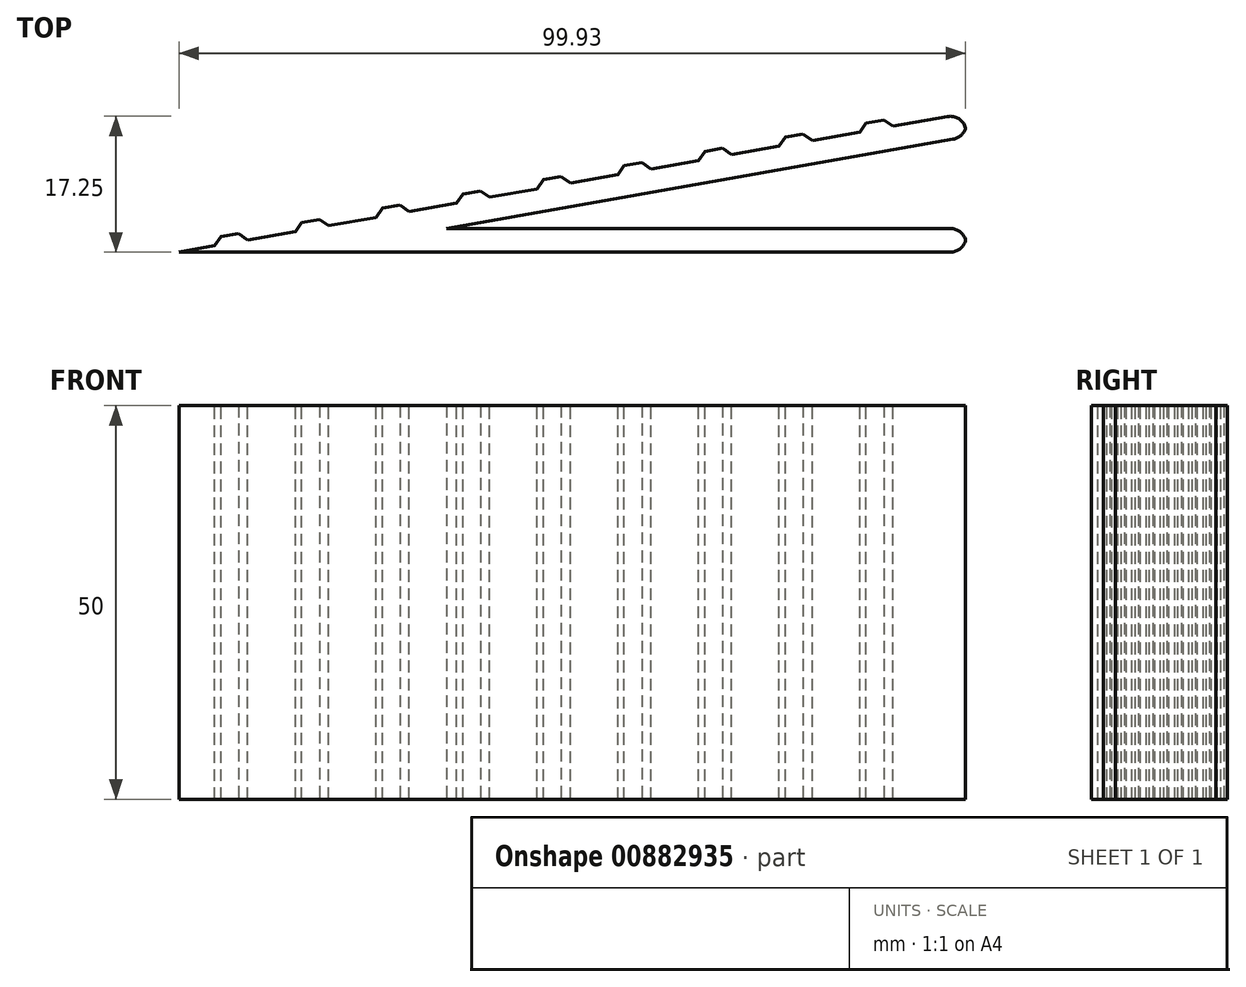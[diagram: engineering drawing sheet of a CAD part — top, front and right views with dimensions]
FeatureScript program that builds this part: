
annotation { "Feature Type Name" : "Feature", "Feature Type Description" : "" }
export const myFeature = defineFeature(function(context is Context, id is Id, definition is map)
    precondition{}
    {
        {
            var Q0;
            Q0=qCreatedBy(makeId("Top.planeOp"),FACE);
            var sketch = newSketch(context, id + "F0", { "sketchPlane" : qUnion([Q0])});
            skLineSegment(sketch, "E0", {"start": v(46.9, 0) * mm, "end": v(-53.1, 0) * mm});
            skLineSegment(sketch, "E1", {"start": v(-53.1, 0) * mm, "end": v(46.9, 17.63) * mm});
            skLineSegment(sketch, "E2", {"start": v(46.9, 3) * mm, "end": v(-19.07, 3) * mm});
            skLineSegment(sketch, "E3", {"start": v(-19.07, 3) * mm, "end": v(46.9, 14.63) * mm});
            skLineSegment(sketch, "E4", {"start": v(46.9, 14.63) * mm, "end": v(46.9, 17.63) * mm});
            skLineSegment(sketch, "E5", {"start": v(46.9, 3) * mm, "end": v(46.9, 0) * mm});
            skSolve(sketch);
        }
        {
            var Q0;
            Q0=makeQuery(id+"F0.imprint","IMPRINT",FACE,{"disambiguationData":[TD([[makeQuery(id+"F0.imprint","IMPRINT",EDGE,{"derivedFrom":sQuery(id+"F0.wireOp",EDGE,"E0")}),-1.0]])]});
            extrude(context, id + "F1", {"entities" : qUnion([Q0]), "depth" : 50 * mm, "offsetDistance" : 25 * mm});
        }
        {
            var Q0;
            Q0=makeQuery(id+"F1.opExtrude","SWEPT_EDGE",EDGE,{"disambiguationData":[OSD([sQuery(id+"F0.wireOp",EDGE,"E1"),sQuery(id+"F0.wireOp",EDGE,"E4")])]});
            var Q1;
            Q1=makeQuery(id+"F1.opExtrude","SWEPT_EDGE",EDGE,{"disambiguationData":[OSD([sQuery(id+"F0.wireOp",EDGE,"E3"),sQuery(id+"F0.wireOp",EDGE,"E4")])]});
            var Q2;
            Q2=makeQuery(id+"F1.opExtrude","SWEPT_EDGE",EDGE,{"disambiguationData":[OSD([sQuery(id+"F0.wireOp",EDGE,"E2"),sQuery(id+"F0.wireOp",EDGE,"E5")])]});
            var Q3;
            Q3=makeQuery(id+"F1.opExtrude","SWEPT_EDGE",EDGE,{"disambiguationData":[OSD([sQuery(id+"F0.wireOp",EDGE,"E0"),sQuery(id+"F0.wireOp",EDGE,"E5")])]});
            fillet(context, id + "F2", {"entities" : qUnion([Q0, Q1, Q2, Q3]), "radius" : 2 * mm, "tangentPropagation" : true, "allowEdgeOverflow" : false});
        }
        {
            var Q0;
            Q0=makeQuery(id+"F1.opExtrude","SWEPT_FACE",FACE,{"disambiguationData":[OSD([sQuery(id+"F0.wireOp",EDGE,"E1")])]});
            var sketch = newSketch(context, id + "F3", { "sketchPlane" : qUnion([Q0])});
            skLineSegment(sketch, "E6.bottom", {"start": v(47.67, 0) * mm, "end": v(43.4, 0) * mm});
            skLineSegment(sketch, "E6.top", {"start": v(47.67, 50) * mm, "end": v(43.4, 50) * mm});
            skLineSegment(sketch, "E6.left", {"start": v(47.67, 0) * mm, "end": v(47.67, 50) * mm});
            skLineSegment(sketch, "E6.right", {"start": v(43.4, 0) * mm, "end": v(43.4, 50) * mm});
            skLineSegment(sketch, "E7.1.0.0", {"start": v(33, 0) * mm, "end": v(33, 50) * mm});
            skLineSegment(sketch, "E7.1.0.1", {"start": v(37.27, 0) * mm, "end": v(37.27, 50) * mm});
            skLineSegment(sketch, "E7.1.0.2", {"start": v(37.27, 0) * mm, "end": v(33, 0) * mm});
            skLineSegment(sketch, "E7.1.0.3", {"start": v(37.27, 50) * mm, "end": v(33, 50) * mm});
            skLineSegment(sketch, "E7.2.0.0", {"start": v(22.6, 0) * mm, "end": v(22.6, 50) * mm});
            skLineSegment(sketch, "E7.2.0.1", {"start": v(26.87, 0) * mm, "end": v(26.87, 50) * mm});
            skLineSegment(sketch, "E7.2.0.2", {"start": v(26.87, 0) * mm, "end": v(22.6, 0) * mm});
            skLineSegment(sketch, "E7.2.0.3", {"start": v(26.87, 50) * mm, "end": v(22.6, 50) * mm});
            skLineSegment(sketch, "E7.3.0.0", {"start": v(12.2, 0) * mm, "end": v(12.2, 50) * mm});
            skLineSegment(sketch, "E7.3.0.1", {"start": v(16.47, 0) * mm, "end": v(16.47, 50) * mm});
            skLineSegment(sketch, "E7.3.0.2", {"start": v(16.47, 0) * mm, "end": v(12.2, 0) * mm});
            skLineSegment(sketch, "E7.3.0.3", {"start": v(16.47, 50) * mm, "end": v(12.2, 50) * mm});
            skLineSegment(sketch, "E7.4.0.0", {"start": v(1.8, 0) * mm, "end": v(1.8, 50) * mm});
            skLineSegment(sketch, "E7.4.0.1", {"start": v(6.07, 0) * mm, "end": v(6.07, 50) * mm});
            skLineSegment(sketch, "E7.4.0.2", {"start": v(6.07, 0) * mm, "end": v(1.8, 0) * mm});
            skLineSegment(sketch, "E7.4.0.3", {"start": v(6.07, 50) * mm, "end": v(1.8, 50) * mm});
            skLineSegment(sketch, "E7.5.0.0", {"start": v(-8.6, 0) * mm, "end": v(-8.6, 50) * mm});
            skLineSegment(sketch, "E7.5.0.1", {"start": v(-4.33, 0) * mm, "end": v(-4.33, 50) * mm});
            skLineSegment(sketch, "E7.5.0.2", {"start": v(-4.33, 0) * mm, "end": v(-8.6, 0) * mm});
            skLineSegment(sketch, "E7.5.0.3", {"start": v(-4.33, 50) * mm, "end": v(-8.6, 50) * mm});
            skLineSegment(sketch, "E7.6.0.0", {"start": v(-19, 0) * mm, "end": v(-19, 50) * mm});
            skLineSegment(sketch, "E7.6.0.1", {"start": v(-14.73, 0) * mm, "end": v(-14.73, 50) * mm});
            skLineSegment(sketch, "E7.6.0.2", {"start": v(-14.73, 0) * mm, "end": v(-19, 0) * mm});
            skLineSegment(sketch, "E7.6.0.3", {"start": v(-14.73, 50) * mm, "end": v(-19, 50) * mm});
            skLineSegment(sketch, "E7.7.0.0", {"start": v(-29.4, 0) * mm, "end": v(-29.4, 50) * mm});
            skLineSegment(sketch, "E7.7.0.1", {"start": v(-25.13, 0) * mm, "end": v(-25.13, 50) * mm});
            skLineSegment(sketch, "E7.7.0.2", {"start": v(-25.13, 0) * mm, "end": v(-29.4, 0) * mm});
            skLineSegment(sketch, "E7.7.0.3", {"start": v(-25.13, 50) * mm, "end": v(-29.4, 50) * mm});
            skLineSegment(sketch, "E7.8.0.0", {"start": v(-39.8, 0) * mm, "end": v(-39.8, 50) * mm});
            skLineSegment(sketch, "E7.8.0.1", {"start": v(-35.53, 0) * mm, "end": v(-35.53, 50) * mm});
            skLineSegment(sketch, "E7.8.0.2", {"start": v(-35.53, 0) * mm, "end": v(-39.8, 0) * mm});
            skLineSegment(sketch, "E7.8.0.3", {"start": v(-35.53, 50) * mm, "end": v(-39.8, 50) * mm});
            skLineSegment(sketch, "E7.direction1", {"start": v(43.4, 0) * mm, "end": v(33, 0) * mm, "construction": true});
            skSolve(sketch);
        }
        {
            var Q0;
            Q0 = qSketchRegion(id + "F3", true);
            extrude(context, id + "F4", {"entities" : qUnion([Q0]), "operationType" : NewBodyOperationType.ADD, "depth" : 1 * mm, "offsetDistance" : 25 * mm});
        }
        {
            var Q0;
            Q0=makeQuery(id+"F4.opExtrude","CAP_EDGE",EDGE,{"disambiguationData":[OSD([sQuery(id+"F3.wireOp",EDGE,"E6.left")])],"isStart":false});
            var Q1;
            Q1=makeQuery(id+"F4.opExtrude","CAP_EDGE",EDGE,{"disambiguationData":[OSD([sQuery(id+"F3.wireOp",EDGE,"E6.right")])],"isStart":false});
            var Q2;
            Q2=makeQuery(id+"F4.opExtrude","CAP_EDGE",EDGE,{"disambiguationData":[OSD([sQuery(id+"F3.wireOp",EDGE,"E7.1.0.1")])],"isStart":false});
            var Q3;
            Q3=makeQuery(id+"F4.opExtrude","CAP_EDGE",EDGE,{"disambiguationData":[OSD([sQuery(id+"F3.wireOp",EDGE,"E7.1.0.0")])],"isStart":false});
            var Q4;
            Q4=makeQuery(id+"F4.opExtrude","CAP_EDGE",EDGE,{"disambiguationData":[OSD([sQuery(id+"F3.wireOp",EDGE,"E7.2.0.1")])],"isStart":false});
            var Q5;
            Q5=makeQuery(id+"F4.opExtrude","CAP_EDGE",EDGE,{"disambiguationData":[OSD([sQuery(id+"F3.wireOp",EDGE,"E7.2.0.0")])],"isStart":false});
            var Q6;
            Q6=makeQuery(id+"F4.opExtrude","CAP_EDGE",EDGE,{"disambiguationData":[OSD([sQuery(id+"F3.wireOp",EDGE,"E7.3.0.1")])],"isStart":false});
            var Q7;
            Q7=makeQuery(id+"F4.opExtrude","CAP_EDGE",EDGE,{"disambiguationData":[OSD([sQuery(id+"F3.wireOp",EDGE,"E7.3.0.0")])],"isStart":false});
            var Q8;
            Q8=makeQuery(id+"F4.opExtrude","CAP_EDGE",EDGE,{"disambiguationData":[OSD([sQuery(id+"F3.wireOp",EDGE,"E7.4.0.1")])],"isStart":false});
            var Q9;
            Q9=makeQuery(id+"F4.opExtrude","CAP_EDGE",EDGE,{"disambiguationData":[OSD([sQuery(id+"F3.wireOp",EDGE,"E7.4.0.0")])],"isStart":false});
            var Q10;
            Q10=makeQuery(id+"F4.opExtrude","CAP_EDGE",EDGE,{"disambiguationData":[OSD([sQuery(id+"F3.wireOp",EDGE,"E7.5.0.1")])],"isStart":false});
            var Q11;
            Q11=makeQuery(id+"F4.opExtrude","CAP_EDGE",EDGE,{"disambiguationData":[OSD([sQuery(id+"F3.wireOp",EDGE,"E7.5.0.0")])],"isStart":false});
            var Q12;
            Q12=makeQuery(id+"F4.opExtrude","CAP_EDGE",EDGE,{"disambiguationData":[OSD([sQuery(id+"F3.wireOp",EDGE,"E7.6.0.1")])],"isStart":false});
            var Q13;
            Q13=makeQuery(id+"F4.opExtrude","CAP_EDGE",EDGE,{"disambiguationData":[OSD([sQuery(id+"F3.wireOp",EDGE,"E7.6.0.0")])],"isStart":false});
            var Q14;
            Q14=makeQuery(id+"F4.opExtrude","CAP_EDGE",EDGE,{"disambiguationData":[OSD([sQuery(id+"F3.wireOp",EDGE,"E7.7.0.1")])],"isStart":false});
            var Q15;
            Q15=makeQuery(id+"F4.opExtrude","CAP_EDGE",EDGE,{"disambiguationData":[OSD([sQuery(id+"F3.wireOp",EDGE,"E7.7.0.0")])],"isStart":false});
            var Q16;
            Q16=makeQuery(id+"F4.opExtrude","CAP_EDGE",EDGE,{"disambiguationData":[OSD([sQuery(id+"F3.wireOp",EDGE,"E7.8.0.1")])],"isStart":false});
            var Q17;
            Q17=makeQuery(id+"F4.opExtrude","CAP_EDGE",EDGE,{"disambiguationData":[OSD([sQuery(id+"F3.wireOp",EDGE,"E7.8.0.0")])],"isStart":false});
            chamfer(context, id + "F5", {"entities" : qUnion([Q0, Q1, Q2, Q3, Q4, Q5, Q6, Q7, Q8, Q9, Q10, Q11, Q12, Q13, Q14, Q15, Q16, Q17]), "width" : 1 * mm, "tangentPropagation" : true});
        }
    });
